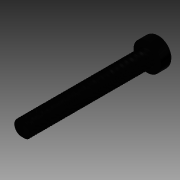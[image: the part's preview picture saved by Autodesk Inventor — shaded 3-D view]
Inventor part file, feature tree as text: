
AUTODESK INVENTOR PART (.ipt)
format: ipt  version: 2013 (Build 170138000, 138)  size: 2,788,864 bytes
history: native  units: mm
features: extrude x1, imported_body x1
ambient origin geometry x8: Origin, YZ Plane, XZ Plane, XY Plane, X Axis, Y Axis, Z Axis, Center Point
feature tree (2):
  extrude  "Extrude3"  [1 undecoded]
  imported_body  "Base1"
note: 1 required parameter value undecoded (feature->parameter linkage not recoverable at this tier; creation-order binding heuristic only, values carry confidence <= 0.55)
